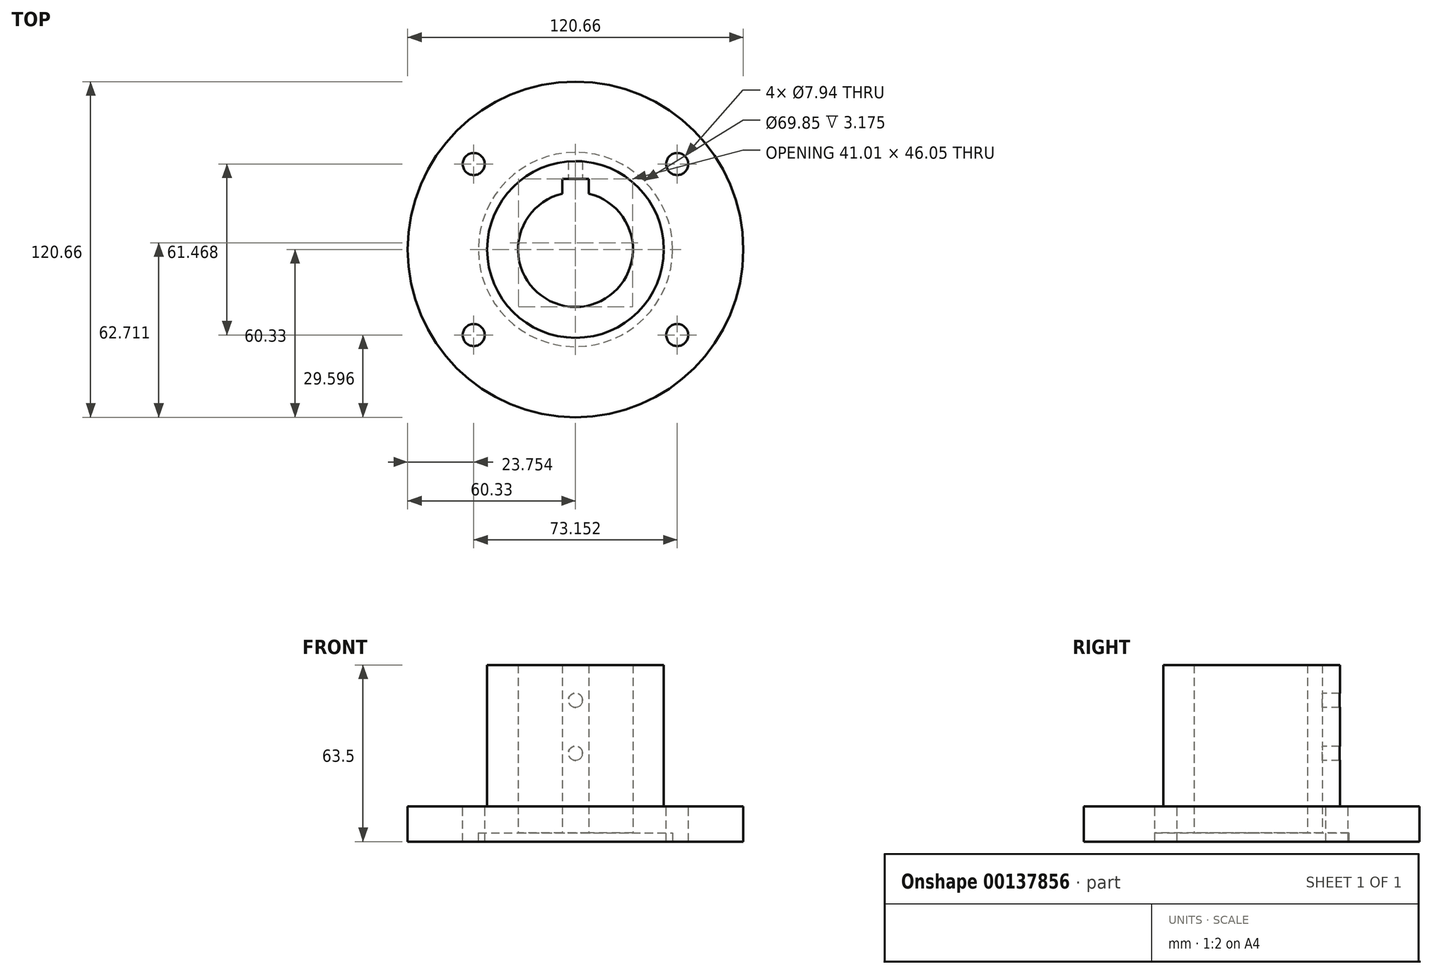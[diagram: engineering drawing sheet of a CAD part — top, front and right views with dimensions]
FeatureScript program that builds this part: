
annotation { "Feature Type Name" : "Feature", "Feature Type Description" : "" }
export const myFeature = defineFeature(function(context is Context, id is Id, definition is map)
    precondition{}
    {
        {
            var Q0;
            Q0=qCreatedBy(makeId("Top.planeOp"),FACE);
            var sketch = newSketch(context, id + "F0", { "sketchPlane" : qUnion([Q0])});
            skCircle(sketch, "E0", {"center": v(0, 0) * mm, "radius": 31.75 * mm});
            skCircle(sketch, "E1", {"center": v(0, 0) * mm, "radius": 20.64 * mm});
            skCircle(sketch, "E2", {"center": v(0, 0) * mm, "radius": 60.33 * mm});
            skLineSegment(sketch, "E3.bottom", {"start": v(4.76, 25.4) * mm, "end": v(-4.76, 25.4) * mm});
            skLineSegment(sketch, "E3.top", {"start": v(4.76, 15.88) * mm, "end": v(-4.76, 15.88) * mm});
            skLineSegment(sketch, "E3.left", {"start": v(4.76, 25.4) * mm, "end": v(4.76, 15.88) * mm});
            skLineSegment(sketch, "E3.right", {"start": v(-4.76, 25.4) * mm, "end": v(-4.76, 15.88) * mm});
            skPoint(sketch, "E3.middle", {"position": v(0, 20.64) * mm});
            skPoint(sketch, "E4", {"position": v(36.58, 30.73) * mm});
            skPoint(sketch, "E5.0.1.0", {"position": v(36.58, -30.73) * mm});
            skPoint(sketch, "E5.1.0.0", {"position": v(-36.58, 30.73) * mm});
            skPoint(sketch, "E5.1.1.0", {"position": v(-36.58, -30.73) * mm});
            skLineSegment(sketch, "E5.direction1", {"start": v(36.58, 30.73) * mm, "end": v(-36.58, 30.73) * mm, "construction": true});
            skLineSegment(sketch, "E5.direction2", {"start": v(36.58, 30.73) * mm, "end": v(36.58, -30.73) * mm, "construction": true});
            skSolve(sketch);
        }
        {
            var Q0;
            Q0=makeQuery(id+"F0.imprint","IMPRINT",FACE,{"disambiguationData":[TD([[makeQuery(id+"F0.imprint","IMPRINT",EDGE,{"derivedFrom":sQuery(id+"F0.wireOp",EDGE,"E0")}),1.0]])]});
            extrude(context, id + "F1", {"entities" : qUnion([Q0]), "depth" : 50.8 * mm});
        }
        {
            var Q0;
            Q0=makeQuery(id+"F0.imprint","IMPRINT",FACE,{"disambiguationData":[TD([[makeQuery(id+"F0.imprint","IMPRINT",EDGE,{"derivedFrom":sQuery(id+"F0.wireOp",EDGE,"E0")}),-1.0]])]});
            var Q1;
            Q1=makeQuery(id+"F0.imprint","IMPRINT",FACE,{"disambiguationData":[TD([[makeQuery(id+"F0.imprint","IMPRINT",EDGE,{"derivedFrom":sQuery(id+"F0.wireOp",EDGE,"E0")}),1.0]])]});
            extrude(context, id + "F2", {"entities" : qUnion([Q0, Q1]), "operationType" : NewBodyOperationType.ADD, "oppositeDirection" : true, "depth" : 12.7 * mm});
        }
        {
            var Q0;
            Q0=qCreatedBy(makeId("Front.planeOp"),FACE);
            var sketch = newSketch(context, id + "F3", { "sketchPlane" : qUnion([Q0])});
            skPoint(sketch, "E6", {"position": v(0, 19.05) * mm});
            skPoint(sketch, "E7", {"position": v(0, 38.1) * mm});
            skSolve(sketch);
        }
        {
            var Q0;
            Q0=sQuery(id+"F3.wireOp",VERTEX,"E7");
            var Q1;
            Q1=sQuery(id+"F3.wireOp",VERTEX,"E6");
            var Q2;
            Q2=makeQuery(id+"F1.opExtrude","SWEPT_BODY",BODY,{"disambiguationData":[OSD([sQuery(id+"F0.wireOp",EDGE,"E0"),sQuery(id+"F0.wireOp",EDGE,"E1"),sQuery(id+"F0.wireOp",EDGE,"E3.bottom"),sQuery(id+"F0.wireOp",EDGE,"E3.left"),sQuery(id+"F0.wireOp",EDGE,"E3.right")])]});
            hole(context, id + "F4", {"style" : HoleStyle.SIMPLE, "endStyle" : HoleEndStyle.THROUGH, "standardTappedOrClearance" : lookupTablePath({ "standard" : "ANSI", "engagement" : "75%", "pitch" : "20 tpi", "size" : "1/4", "type" : "Tapped" }), "standardBlindInLast" : lookupTablePath({ "standard" : "ANSI", "engagement" : "75%", "pitch" : "20 tpi", "size" : "1/4", "type" : "Tapped" }), "holeDiameter" : 5.1 * mm, "locations" : qUnion([Q0, Q1]), "scope" : qUnion([Q2]), "isTappedThrough" : true, "majorDiameter" : 6.35 * mm, "showTappedDepth" : true});
        }
        {
            var Q0;
            Q0=makeQuery(id+"F2.opExtrude","CAP_FACE",FACE,{"disambiguationData":[OSD([sQuery(id+"F0.wireOp",EDGE,"E1"),sQuery(id+"F0.wireOp",EDGE,"E2"),sQuery(id+"F0.wireOp",EDGE,"E3.bottom"),sQuery(id+"F0.wireOp",EDGE,"E3.left"),sQuery(id+"F0.wireOp",EDGE,"E3.right"),sQuery(id+"F0.wireOp",EDGE,"vrSMndVF-ONKF-yYun-SgnW-vLCMi54Z5bI7"),sQuery(id+"F0.wireOp",EDGE,"2e7be013-f15b-4008-9f86-7416d8b2c7d0.0.1.0"),sQuery(id+"F0.wireOp",EDGE,"2e7be013-f15b-4008-9f86-7416d8b2c7d0.1.0.0"),sQuery(id+"F0.wireOp",EDGE,"2e7be013-f15b-4008-9f86-7416d8b2c7d0.1.1.0")])],"isStart":false});
            var sketch = newSketch(context, id + "F5", { "sketchPlane" : qUnion([Q0])});
            skCircle(sketch, "E8", {"center": v(0, 0) * mm, "radius": 34.93 * mm});
            skSolve(sketch);
        }
        {
            var Q0;
            Q0=makeQuery(id+"F5.imprint","IMPRINT",FACE,{"disambiguationData":[TD([[makeQuery(id+"F5.imprint","IMPRINT",EDGE,{"derivedFrom":sQuery(id+"F5.wireOp",EDGE,"E8")}),1.0]])]});
            extrude(context, id + "F6", {"entities" : qUnion([Q0]), "operationType" : NewBodyOperationType.REMOVE, "oppositeDirection" : true, "depth" : 3.17 * mm});
        }
        {
            var Q0;
            Q0=sQuery(id+"F0.wireOp",VERTEX,"E5.1.1.0");
            var Q1;
            Q1=sQuery(id+"F0.wireOp",VERTEX,"E5.0.1.0");
            var Q2;
            Q2=sQuery(id+"F0.wireOp",VERTEX,"E4");
            var Q3;
            Q3=sQuery(id+"F0.wireOp",VERTEX,"E5.1.0.0");
            var Q4;
            Q4=makeQuery(id+"F1.opExtrude","SWEPT_BODY",BODY,{"disambiguationData":[OSD([sQuery(id+"F0.wireOp",EDGE,"E0"),sQuery(id+"F0.wireOp",EDGE,"E1"),sQuery(id+"F0.wireOp",EDGE,"E3.bottom"),sQuery(id+"F0.wireOp",EDGE,"E3.left"),sQuery(id+"F0.wireOp",EDGE,"E3.right")])]});
            hole(context, id + "F7", {"style" : HoleStyle.SIMPLE, "endStyle" : HoleEndStyle.THROUGH, "standardTappedOrClearance" : lookupTablePath({ "standard" : "ANSI", "engagement" : "75%", "pitch" : "16 tpi", "size" : "3/8", "type" : "Tapped" }), "standardBlindInLast" : lookupTablePath({ "standard" : "ANSI", "engagement" : "75%", "pitch" : "16 tpi", "size" : "3/8", "type" : "Tapped" }), "holeDiameter" : 7.94 * mm, "locations" : qUnion([Q0, Q1, Q2, Q3]), "scope" : qUnion([Q4]), "isTappedThrough" : true, "majorDiameter" : 9.53 * mm, "showTappedDepth" : true});
        }
    });
